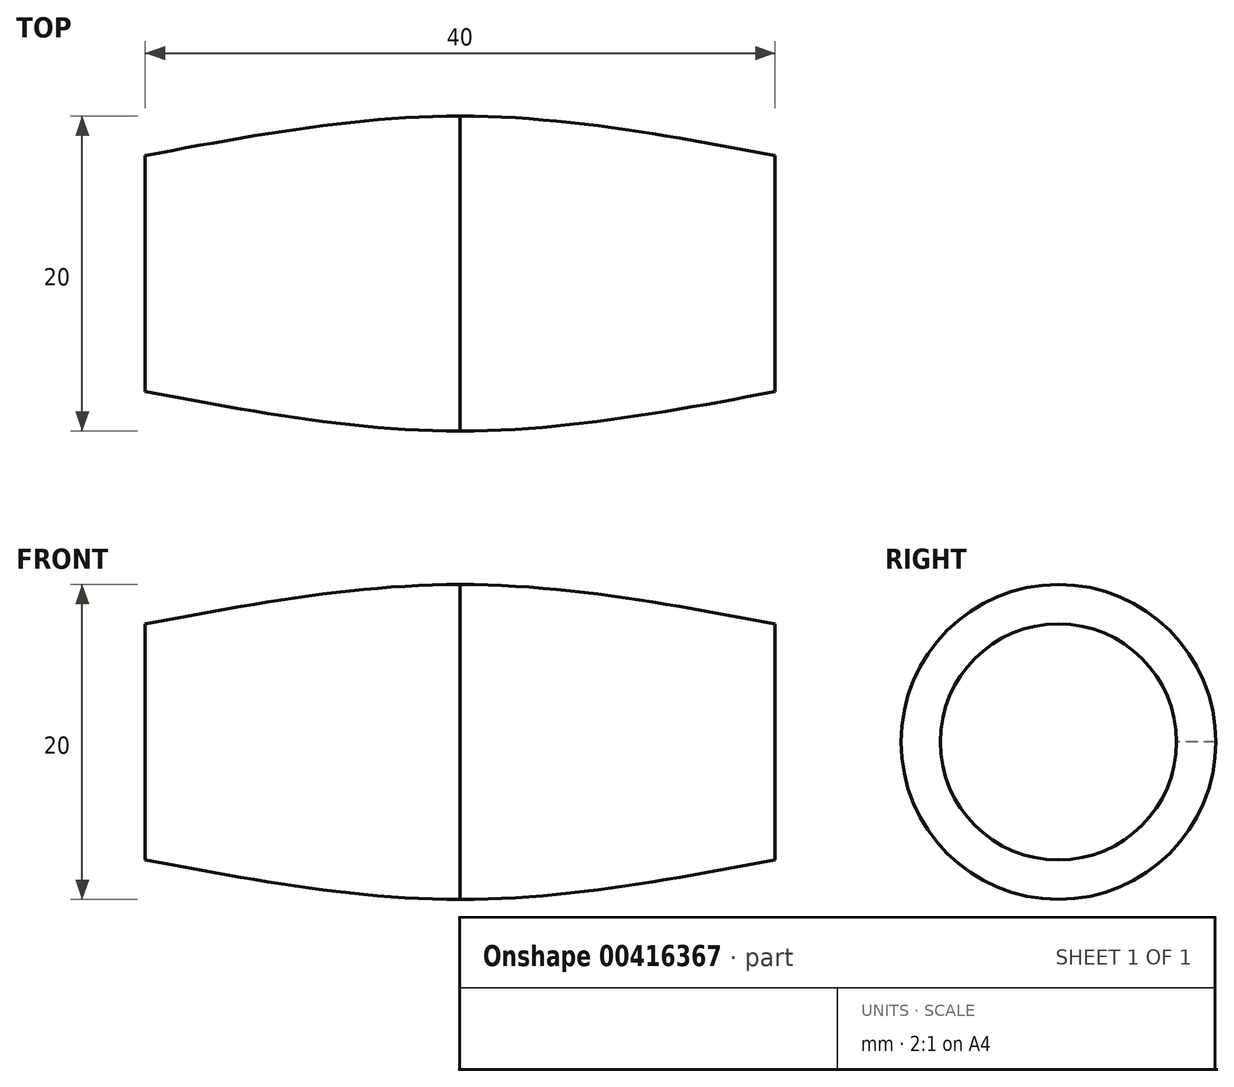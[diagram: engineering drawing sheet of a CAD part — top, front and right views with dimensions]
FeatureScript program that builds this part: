
annotation { "Feature Type Name" : "Feature", "Feature Type Description" : "" }
export const myFeature = defineFeature(function(context is Context, id is Id, definition is map)
    precondition{}
    {
        {
            var Q0;
            Q0=qCreatedBy(makeId("Front.planeOp"),FACE);
            var sketch = newSketch(context, id + "F0", { "sketchPlane" : qUnion([Q0])});
            skLineSegment(sketch, "E0", {"start": v(0, 0) * mm, "end": v(20, 0) * mm});
            skLineSegment(sketch, "E1", {"start": v(20, 0) * mm, "end": v(0, 0) * mm});
            skLineSegment(sketch, "E2", {"start": v(0, 0) * mm, "end": v(0, 0) * mm});
            skLineSegment(sketch, "E3", {"start": v(0, 0) * mm, "end": v(-20, 0) * mm});
            skLineSegment(sketch, "E4", {"start": v(-20, 0) * mm, "end": v(-20, 7.5) * mm, "construction": true});
            skLineSegment(sketch, "E5", {"start": v(0, 0) * mm, "end": v(0, 10) * mm, "construction": true});
            skLineSegment(sketch, "E6", {"start": v(20, 0) * mm, "end": v(20, 7.5) * mm, "construction": true});
            skLineSegment(sketch, "E7", {"start": v(-20, 0) * mm, "end": v(-20, -7.5) * mm, "construction": true});
            skLineSegment(sketch, "E8", {"start": v(0, 0) * mm, "end": v(0, -10) * mm, "construction": true});
            skLineSegment(sketch, "E9", {"start": v(20, 0) * mm, "end": v(20, -7.5) * mm, "construction": true});
            skFitSpline(sketch, "E10", {"points": [v(-20, 7.5) * mm, v(0, 10) * mm, v(20, 7.5) * mm], "startDerivative": vector(40, 7.5) * mm, "endDerivative": vector(40, -7.5) * mm});
            skFitSpline(sketch, "E11", {"points": [v(-20, -7.5) * mm, v(0, -10) * mm, v(20, -7.5) * mm], "startDerivative": vector(40, -7.5) * mm, "endDerivative": vector(40, 7.5) * mm});
            skSolve(sketch);
        }
        {
            var Q0;
            Q0=qCreatedBy(makeId("Right.planeOp"),FACE);
            cPlane(context, id + "F1", {"entities" : qUnion([Q0]), "cplaneType" : CPlaneType.OFFSET, "offset" : 20 * mm, "width" : 150 * mm, "height" : 150 * mm});
        }
        {
            var Q0;
            Q0=qCreatedBy(makeId("Right.planeOp"),FACE);
            cPlane(context, id + "F2", {"entities" : qUnion([Q0]), "cplaneType" : CPlaneType.OFFSET, "offset" : 20 * mm, "oppositeDirection" : true, "width" : 150 * mm, "height" : 150 * mm});
        }
        {
            var Q0;
            Q0=qCreatedBy(id+"F1.planeOp",FACE);
            var sketch = newSketch(context, id + "F3", { "sketchPlane" : qUnion([Q0])});
            skCircle(sketch, "E12", {"center": v(0, 0) * mm, "radius": 7.5 * mm});
            skSolve(sketch);
        }
        {
            var Q0;
            Q0=qCreatedBy(id+"F2.planeOp",FACE);
            var sketch = newSketch(context, id + "F4", { "sketchPlane" : qUnion([Q0])});
            skCircle(sketch, "E13", {"center": v(0, 0) * mm, "radius": 7.5 * mm});
            skSolve(sketch);
        }
        {
            var Q0;
            Q0=qCreatedBy(makeId("Right.planeOp"),FACE);
            var sketch = newSketch(context, id + "F5", { "sketchPlane" : qUnion([Q0])});
            skCircle(sketch, "E14", {"center": v(0, 0) * mm, "radius": 10 * mm});
            skSolve(sketch);
        }
        {
            var Q0;
            Q0=qCreatedBy(makeId("Top.planeOp"),FACE);
            var sketch = newSketch(context, id + "F6", { "sketchPlane" : qUnion([Q0])});
            skLineSegment(sketch, "E15", {"start": v(0, 0) * mm, "end": v(20, 0) * mm});
            skLineSegment(sketch, "E16", {"start": v(0, 0) * mm, "end": v(-20, 0) * mm});
            skLineSegment(sketch, "E17", {"start": v(-20, 0) * mm, "end": v(-20, 7.5) * mm, "construction": true});
            skLineSegment(sketch, "E18", {"start": v(0, 0) * mm, "end": v(0, 10) * mm, "construction": true});
            skLineSegment(sketch, "E19", {"start": v(20, 0) * mm, "end": v(20, 7.5) * mm, "construction": true});
            skLineSegment(sketch, "E20", {"start": v(-20, 0) * mm, "end": v(-20, -7.5) * mm, "construction": true});
            skLineSegment(sketch, "E21", {"start": v(0, 0) * mm, "end": v(0, -10) * mm, "construction": true});
            skLineSegment(sketch, "E22", {"start": v(20, 0) * mm, "end": v(20, -7.5) * mm, "construction": true});
            skFitSpline(sketch, "E23", {"points": [v(-20, 7.5) * mm, v(0, 10) * mm, v(20, 7.5) * mm], "startDerivative": vector(40, 7.5) * mm, "endDerivative": vector(40, -7.5) * mm});
            skFitSpline(sketch, "E24", {"points": [v(-20, -7.5) * mm, v(0, -10) * mm, v(20, -7.5) * mm], "startDerivative": vector(40, -7.5) * mm, "endDerivative": vector(40, 7.5) * mm});
            skSolve(sketch);
        }
        {
            var Q0;
            Q0=makeQuery(id+"F3.imprint","IMPRINT",FACE,{"disambiguationData":[TD([[makeQuery(id+"F3.imprint","IMPRINT",EDGE,{"derivedFrom":sQuery(id+"F3.wireOp",EDGE,"E12")}),1.0]])]});
            var Q1;
            Q1=makeQuery(id+"F5.imprint","IMPRINT",FACE,{"disambiguationData":[TD([[makeQuery(id+"F5.imprint","IMPRINT",EDGE,{"derivedFrom":sQuery(id+"F5.wireOp",EDGE,"E14")}),1.0]])]});
            var Q2;
            Q2=sQuery(id+"F0.wireOp",EDGE,"E10");
            var Q3;
            Q3=sQuery(id+"F6.wireOp",EDGE,"E23");
            var Q4;
            Q4=sQuery(id+"F6.wireOp",EDGE,"E24");
            var Q5;
            Q5=sQuery(id+"F0.wireOp",EDGE,"E11");
            loft(context, id + "F7", {"addGuides" : true, "sheetProfilesArray" : [{ "sheetProfileEntities" : qUnion([Q0]) }, { "sheetProfileEntities" : qUnion([Q1]) }], "guidesArray" : [{ "guideEntities" : qUnion([Q2]), "guideDerivativeType" : LoftGuideDerivativeType.DEFAULT, "guideDerivativeMagnitude" : 1 }, { "guideEntities" : qUnion([Q3]), "guideDerivativeType" : LoftGuideDerivativeType.DEFAULT, "guideDerivativeMagnitude" : 1 }, { "guideEntities" : qUnion([Q4]), "guideDerivativeType" : LoftGuideDerivativeType.DEFAULT, "guideDerivativeMagnitude" : 1 }, { "guideEntities" : qUnion([Q5]), "guideDerivativeType" : LoftGuideDerivativeType.DEFAULT, "guideDerivativeMagnitude" : 1 }]});
        }
        {
            var Q1;
            Q1=makeQuery(id+"F7.opLoft","CAP_FACE",FACE,{"disambiguationData":[OSD([makeQuery(id+"F5.imprint","IMPRINT",FACE,{"disambiguationData":[TD([[makeQuery(id+"F5.imprint","IMPRINT",EDGE,{"derivedFrom":sQuery(id+"F5.wireOp",EDGE,"E14")}),1.0]])]})])],"isStart":true});
            var Q2;
            Q2=makeQuery(id+"F4.imprint","IMPRINT",FACE,{"disambiguationData":[TD([[makeQuery(id+"F4.imprint","IMPRINT",EDGE,{"derivedFrom":sQuery(id+"F4.wireOp",EDGE,"E13")}),1.0]])]});
            var Q3;
            Q3=makeQuery(id+"F7.opLoft","CAP_FACE",FACE,{"disambiguationData":[OSD([makeQuery(id+"F5.imprint","IMPRINT",FACE,{"disambiguationData":[TD([[makeQuery(id+"F5.imprint","IMPRINT",EDGE,{"derivedFrom":sQuery(id+"F5.wireOp",EDGE,"E14")}),1.0]])]})])],"isStart":true});
            var Q4;
            Q4=makeQuery(id+"F4.imprint","IMPRINT",FACE,{"disambiguationData":[TD([[makeQuery(id+"F4.imprint","IMPRINT",EDGE,{"derivedFrom":sQuery(id+"F4.wireOp",EDGE,"E13")}),1.0]])]});
            var Q5;
            Q5=sQuery(id+"F0.wireOp",EDGE,"E10");
            var Q6;
            Q6=sQuery(id+"F0.wireOp",EDGE,"E11");
            var Q7;
            Q7=sQuery(id+"F6.wireOp",EDGE,"E24");
            var Q8;
            Q8=sQuery(id+"F6.wireOp",EDGE,"E23");
            loft(context, id + "F8", {"operationType" : NewBodyOperationType.ADD, "addGuides" : true, "sheetProfilesArray" : [{ "sheetProfileEntities" : qUnion([Q1]) }, { "sheetProfileEntities" : qUnion([Q2]) }], "wireProfilesArray" : [{ "wireProfileEntities" : qUnion([Q3]) }, { "wireProfileEntities" : qUnion([Q4]) }], "guidesArray" : [{ "guideEntities" : qUnion([Q5]), "guideDerivativeType" : LoftGuideDerivativeType.DEFAULT, "guideDerivativeMagnitude" : 1 }, { "guideEntities" : qUnion([Q6]), "guideDerivativeType" : LoftGuideDerivativeType.DEFAULT, "guideDerivativeMagnitude" : 1 }, { "guideEntities" : qUnion([Q7]), "guideDerivativeType" : LoftGuideDerivativeType.DEFAULT, "guideDerivativeMagnitude" : 1 }, { "guideEntities" : qUnion([Q8]), "guideDerivativeType" : LoftGuideDerivativeType.DEFAULT, "guideDerivativeMagnitude" : 1 }]});
        }
    });
